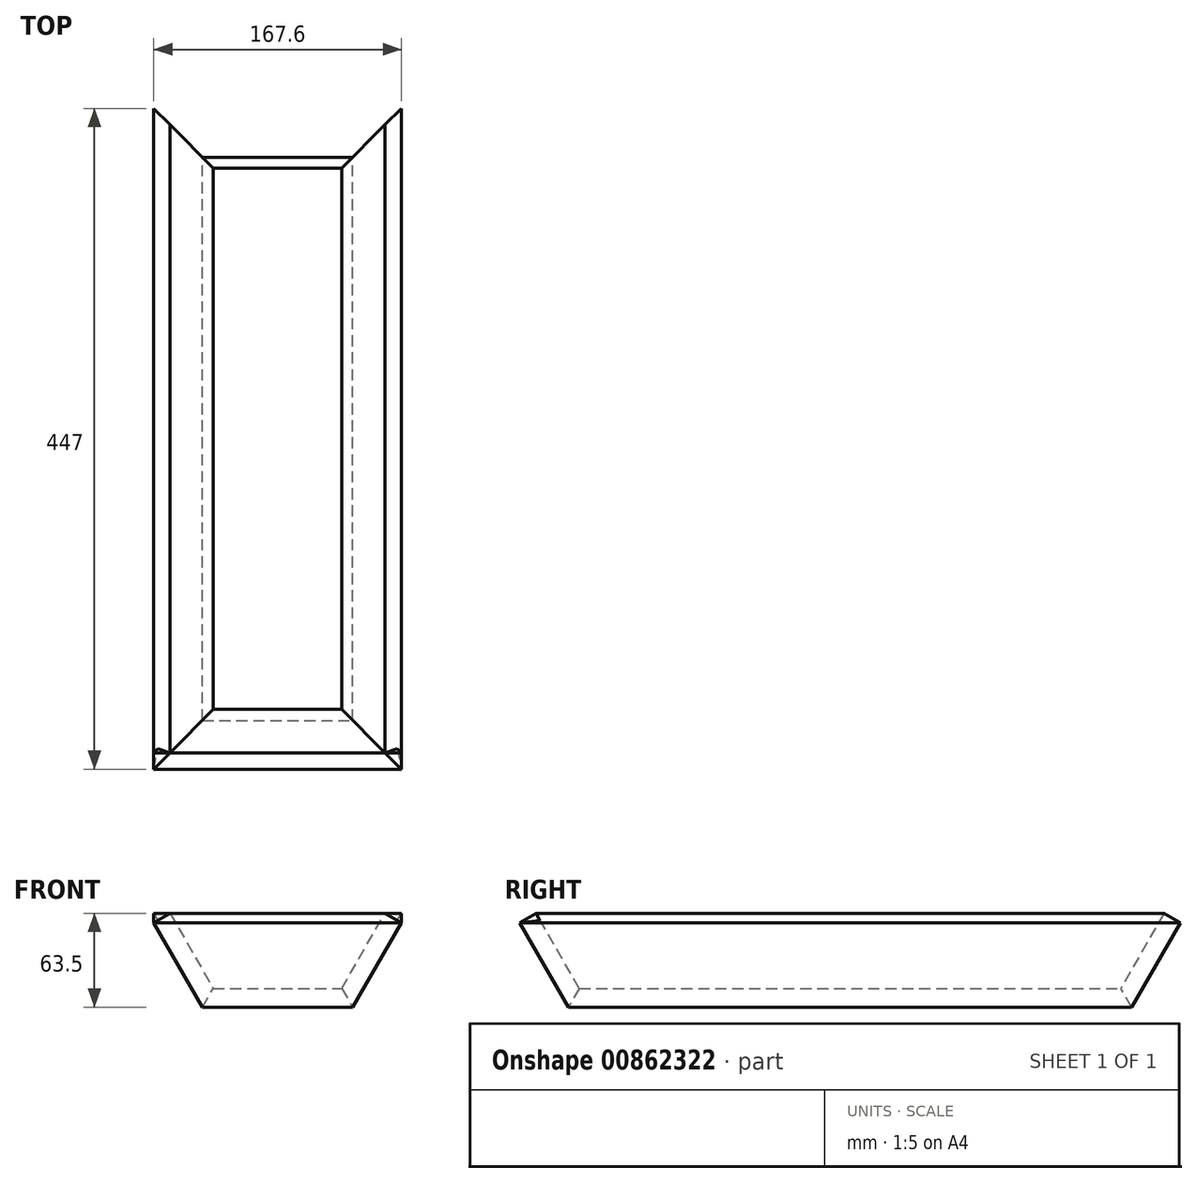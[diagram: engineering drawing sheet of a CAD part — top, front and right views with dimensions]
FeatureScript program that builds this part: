
annotation { "Feature Type Name" : "Feature", "Feature Type Description" : "" }
export const myFeature = defineFeature(function(context is Context, id is Id, definition is map)
    precondition{}
    {
        {
            var Q0;
            Q0=qCreatedBy(makeId("Top.planeOp"),FACE);
            var sketch = newSketch(context, id + "F0", { "sketchPlane" : qUnion([Q0])});
            skLineSegment(sketch, "E0.bottom", {"start": v(-50.8, 190.5) * mm, "end": v(50.8, 190.5) * mm});
            skLineSegment(sketch, "E0.top", {"start": v(-50.8, -190.5) * mm, "end": v(50.8, -190.5) * mm});
            skLineSegment(sketch, "E0.left", {"start": v(-50.8, 190.5) * mm, "end": v(-50.8, -190.5) * mm});
            skLineSegment(sketch, "E0.right", {"start": v(50.8, 190.5) * mm, "end": v(50.8, -190.5) * mm});
            skLineSegment(sketch, "E1", {"start": v(50.8, -190.5) * mm, "end": v(-50.8, 190.5) * mm, "construction": true});
            skSolve(sketch);
        }
        {
            var Q0;
            Q0 = qSketchRegion(id + "F0", true);
            extrude(context, id + "F1", {"entities" : qUnion([Q0]), "depth" : 12.7 * mm, "offsetDistance" : 25.4 * mm, "hasDraft" : true, "draftAngle" : 30 * degree, "draftPullDirection" : true});
        }
        {
            var Q0;
            Q0=qCreatedBy(makeId("Front.planeOp"),FACE);
            var sketch = newSketch(context, id + "F2", { "sketchPlane" : qUnion([Q0])});
            skLineSegment(sketch, "E2", {"start": v(-50.8, 0) * mm, "end": v(-83.8, 57.15) * mm});
            skLineSegment(sketch, "E3", {"start": v(-83.8, 57.15) * mm, "end": v(-72.8, 63.5) * mm});
            skLineSegment(sketch, "E4", {"start": v(-72.8, 63.5) * mm, "end": v(-43.47, 12.7) * mm});
            skLineSegment(sketch, "E5", {"start": v(-43.47, 12.7) * mm, "end": v(-50.8, 0) * mm});
            skSolve(sketch);
        }
        {
            var Q0;
            Q0 = qSketchRegion(id + "F2", true);
            extrude(context, id + "F3", {"entities" : qUnion([Q0]), "endBound" : BoundingType.SYMMETRIC, "depth" : 457.2 * mm, "offsetDistance" : 25.4 * mm, "hasSecondDirection" : true, "secondDirectionOppositeDirection" : true, "secondDirectionDepth" : 50.8 * mm});
        }
        {
            var Q0;
            Q0=makeQuery(id+"F1.opExtrude","CAP_FACE",FACE,{"disambiguationData":[OSD([sQuery(id+"F0.wireOp",EDGE,"E0.bottom"),sQuery(id+"F0.wireOp",EDGE,"E0.top"),sQuery(id+"F0.wireOp",EDGE,"E0.left"),sQuery(id+"F0.wireOp",EDGE,"E0.right")])],"isStart":true});
            var sketch = newSketch(context, id + "F4", { "sketchPlane" : qUnion([Q0])});
            skLineSegment(sketch, "E6", {"start": v(-43.47, -183.17) * mm, "end": v(-274.53, -414.23) * mm});
            skLineSegment(sketch, "E7", {"start": v(-274.53, -414.23) * mm, "end": v(-274.53, 414.23) * mm});
            skLineSegment(sketch, "E8", {"start": v(-274.53, 414.23) * mm, "end": v(-43.47, 183.17) * mm});
            skLineSegment(sketch, "E9", {"start": v(-43.47, 183.17) * mm, "end": v(-43.47, -183.17) * mm});
            skLineSegment(sketch, "E10", {"start": v(-274.53, -414.23) * mm, "end": v(274.53, -414.23) * mm});
            skLineSegment(sketch, "E11", {"start": v(274.53, -414.23) * mm, "end": v(43.47, -183.17) * mm});
            skLineSegment(sketch, "E12", {"start": v(43.47, -183.17) * mm, "end": v(43.47, 183.17) * mm});
            skLineSegment(sketch, "E13", {"start": v(43.47, 183.17) * mm, "end": v(-43.47, 183.17) * mm});
            skLineSegment(sketch, "E14", {"start": v(43.47, 183.17) * mm, "end": v(274.53, 414.23) * mm});
            skLineSegment(sketch, "E15", {"start": v(274.53, 414.23) * mm, "end": v(274.53, -414.23) * mm});
            skLineSegment(sketch, "E16", {"start": v(-274.53, 414.23) * mm, "end": v(274.53, 414.23) * mm});
            skLineSegment(sketch, "E17", {"start": v(-43.47, -183.17) * mm, "end": v(43.47, -183.17) * mm});
            skSolve(sketch);
        }
        {
            var Q0;
            {var subQ2=sQuery(id+"F4.wireOp",EDGE,"E10");Q0=makeQuery(id+"F4.imprint","IMPRINT",FACE,{"disambiguationData":[TD([[makeQuery(id+"F4.imprint","IMPRINT",EDGE,{"derivedFrom":subQ2}),1.0]])]});}
            var Q1;
            {var subQ2=sQuery(id+"F4.wireOp",EDGE,"E15");Q1=makeQuery(id+"F4.imprint","IMPRINT",FACE,{"disambiguationData":[TD([[makeQuery(id+"F4.imprint","IMPRINT",EDGE,{"derivedFrom":subQ2}),-1.0]])]});}
            var Q2;
            {var subQ2=sQuery(id+"F4.wireOp",EDGE,"E16");Q2=makeQuery(id+"F4.imprint","IMPRINT",FACE,{"disambiguationData":[TD([[makeQuery(id+"F4.imprint","IMPRINT",EDGE,{"derivedFrom":subQ2}),-1.0]])]});}
            extrude(context, id + "F5", {"entities" : qUnion([Q0, Q1, Q2]), "operationType" : NewBodyOperationType.REMOVE, "endBound" : BoundingType.THROUGH_ALL, "oppositeDirection" : true, "depth" : 25.4 * mm, "offsetDistance" : 25.4 * mm});
        }
        {
            var Q0;
            Q0=makeQuery(id+"F5.boolean.opBoolean","COPY",FACE,{"derivedFrom":makeQuery(id+"F5.opExtrude","SWEPT_FACE",FACE,{"disambiguationData":[OSD([sQuery(id+"F4.wireOp",EDGE,"E8")])]})});
            var sketch = newSketch(context, id + "F6", { "sketchPlane" : qUnion([Q0])});
            skLineSegment(sketch, "E18", {"start": v(-201.73, 63.5) * mm, "end": v(-160.26, 12.7) * mm});
            skLineSegment(sketch, "E19", {"start": v(-160.26, 12.7) * mm, "end": v(-170.62, 0) * mm});
            skLineSegment(sketch, "E20", {"start": v(-170.62, 0) * mm, "end": v(-217.29, 57.15) * mm});
            skLineSegment(sketch, "E21", {"start": v(-217.29, 57.15) * mm, "end": v(-201.73, 63.5) * mm});
            skSolve(sketch);
        }
        {
            var Q0;
            Q0 = qSketchRegion(id + "F6", true);
            extrude(context, id + "F7", {"entities" : qUnion([Q0]), "operationType" : NewBodyOperationType.REMOVE, "depth" : 25.4 * mm, "offsetDistance" : 25.4 * mm});
        }
        {
            var Q0;
            Q0=makeQuery(id+"F5.boolean.opBoolean","COPY",FACE,{"derivedFrom":makeQuery(id+"F5.opExtrude","SWEPT_FACE",FACE,{"disambiguationData":[OSD([sQuery(id+"F4.wireOp",EDGE,"E6")])]})});
            var sketch = newSketch(context, id + "F8", { "sketchPlane" : qUnion([Q0])});
            skLineSegment(sketch, "E22", {"start": v(201.73, 63.5) * mm, "end": v(217.29, 57.15) * mm});
            skLineSegment(sketch, "E23", {"start": v(217.29, 57.15) * mm, "end": v(170.62, 0) * mm});
            skLineSegment(sketch, "E24", {"start": v(170.62, 0) * mm, "end": v(160.26, 12.7) * mm});
            skLineSegment(sketch, "E25", {"start": v(160.26, 12.7) * mm, "end": v(201.73, 63.5) * mm});
            skSolve(sketch);
        }
        {
            var Q0;
            Q0 = qSketchRegion(id + "F8", true);
            extrude(context, id + "F9", {"entities" : qUnion([Q0]), "operationType" : NewBodyOperationType.REMOVE, "depth" : 25.4 * mm, "offsetDistance" : 25.4 * mm});
        }
        {
            var Q0;
            Q0=makeQuery(id+"F3.opExtrude","SWEPT_BODY",BODY,{"disambiguationData":[OSD([sQuery(id+"F2.wireOp",EDGE,"E2"),sQuery(id+"F2.wireOp",EDGE,"E3"),sQuery(id+"F2.wireOp",EDGE,"E4"),sQuery(id+"F2.wireOp",EDGE,"E5")])]});
            var Q1;
            Q1=qCreatedBy(makeId("Right.planeOp"),FACE);
            mirror(context, id + "F10", {"entities" : qUnion([Q0]), "mirrorPlane" : qUnion([Q1])});
        }
        {
            var Q0;
            Q0=makeQuery(id+"F1.opExtrude","CAP_VERTEX",VERTEX,{"disambiguationData":[OSD([sQuery(id+"F0.wireOp",EDGE,"E0.bottom"),sQuery(id+"F0.wireOp",EDGE,"E0.right")])],"isStart":true});
            var Q1;
            Q1=makeQuery(id+"F1.opExtrude","CAP_VERTEX",VERTEX,{"disambiguationData":[OSD([sQuery(id+"F0.wireOp",EDGE,"E0.bottom"),sQuery(id+"F0.wireOp",EDGE,"E0.left")])],"isStart":true});
            var Q2;
            Q2=makeQuery(id+"F5.boolean.opBoolean","INTERSECT",VERTEX,{"derivedFrom":[makeQuery(id+"F3.opExtrude","SWEPT_FACE",FACE,{"disambiguationData":[OSD([sQuery(id+"F2.wireOp",EDGE,"E2")])]}),makeQuery(id+"F3.opExtrude","SWEPT_FACE",FACE,{"disambiguationData":[OSD([sQuery(id+"F2.wireOp",EDGE,"E3")])]}),makeQuery(id+"F5.opExtrude","SWEPT_FACE",FACE,{"disambiguationData":[OSD([sQuery(id+"F4.wireOp",EDGE,"E6")])]})]});
            cPlane(context, id + "F11", {"entities" : qUnion([Q0, Q1, Q2]), "cplaneType" : CPlaneType.THREE_POINT, "offset" : 25.4 * mm, "width" : 152.4 * mm, "height" : 152.4 * mm});
        }
        {
            var Q0;
            Q0=qCreatedBy(id+"F11.planeOp",FACE);
            var sketch = newSketch(context, id + "F12", { "sketchPlane" : qUnion([Q0])});
            skLineSegment(sketch, "E26", {"start": v(-83.8, 161.24) * mm, "end": v(-50.8, 95.25) * mm});
            skLineSegment(sketch, "E27", {"start": v(-50.8, 95.25) * mm, "end": v(50.8, 95.25) * mm});
            skLineSegment(sketch, "E28", {"start": v(50.8, 95.25) * mm, "end": v(83.8, 161.24) * mm});
            skLineSegment(sketch, "E29", {"start": v(83.8, 161.24) * mm, "end": v(-83.8, 161.24) * mm});
            skSolve(sketch);
        }
        {
            var Q0;
            Q0 = qSketchRegion(id + "F12", true);
            extrude(context, id + "F13", {"entities" : qUnion([Q0]), "depth" : 12.7 * mm, "offsetDistance" : 25.4 * mm});
        }
        {
            var Q0;
            Q0=makeQuery(id+"F1.opExtrude","SWEPT_BODY",BODY,{"disambiguationData":[OSD([sQuery(id+"F0.wireOp",EDGE,"E0.bottom"),sQuery(id+"F0.wireOp",EDGE,"E0.top"),sQuery(id+"F0.wireOp",EDGE,"E0.left"),sQuery(id+"F0.wireOp",EDGE,"E0.right")])]});
            var Q1;
            Q1=makeQuery(id+"F10.opPattern","COPY",BODY,{"derivedFrom":makeQuery(id+"F3.opExtrude","SWEPT_BODY",BODY,{"disambiguationData":[OSD([sQuery(id+"F2.wireOp",EDGE,"E2"),sQuery(id+"F2.wireOp",EDGE,"E3"),sQuery(id+"F2.wireOp",EDGE,"E4"),sQuery(id+"F2.wireOp",EDGE,"E5")])]}),"instanceName":"1"});
            var Q2;
            Q2=makeQuery(id+"F3.opExtrude","SWEPT_BODY",BODY,{"disambiguationData":[OSD([sQuery(id+"F2.wireOp",EDGE,"E2"),sQuery(id+"F2.wireOp",EDGE,"E3"),sQuery(id+"F2.wireOp",EDGE,"E4"),sQuery(id+"F2.wireOp",EDGE,"E5")])]});
            var Q3;
            Q3=makeQuery(id+"F13.opExtrude","SWEPT_BODY",BODY,{"disambiguationData":[OSD([sQuery(id+"F12.wireOp",EDGE,"E26"),sQuery(id+"F12.wireOp",EDGE,"E27"),sQuery(id+"F12.wireOp",EDGE,"E28"),sQuery(id+"F12.wireOp",EDGE,"E29")])]});
            booleanBodies(context, id + "F14", {"operationType" : BooleanOperationType.SUBTRACTION, "tools" : qUnion([Q0, Q1, Q2]), "targets" : qUnion([Q3]), "keepTools" : true});
        }
        {
            var Q0;
            Q0=makeQuery(id+"F14.opBoolean","SPLIT",BODY,{"disambiguationData":[OD(0.0)],"derivedFrom":makeQuery(id+"F13.opExtrude","SWEPT_BODY",BODY,{"disambiguationData":[OSD([sQuery(id+"F12.wireOp",EDGE,"E26"),sQuery(id+"F12.wireOp",EDGE,"E27"),sQuery(id+"F12.wireOp",EDGE,"E28"),sQuery(id+"F12.wireOp",EDGE,"E29")])]})});
            var Q1;
            Q1=qCreatedBy(makeId("Front.planeOp"),FACE);
            mirror(context, id + "F15", {"entities" : qUnion([Q0]), "mirrorPlane" : qUnion([Q1])});
        }
        {
            var Q0;
            Q0=makeQuery(id+"F14.opBoolean","SPLIT",BODY,{"disambiguationData":[OD(2.0)],"derivedFrom":makeQuery(id+"F13.opExtrude","SWEPT_BODY",BODY,{"disambiguationData":[OSD([sQuery(id+"F12.wireOp",EDGE,"E26"),sQuery(id+"F12.wireOp",EDGE,"E27"),sQuery(id+"F12.wireOp",EDGE,"E28"),sQuery(id+"F12.wireOp",EDGE,"E29")])]})});
            var Q1;
            Q1=makeQuery(id+"F14.opBoolean","SPLIT",BODY,{"disambiguationData":[OD(1.0)],"derivedFrom":makeQuery(id+"F13.opExtrude","SWEPT_BODY",BODY,{"disambiguationData":[OSD([sQuery(id+"F12.wireOp",EDGE,"E26"),sQuery(id+"F12.wireOp",EDGE,"E27"),sQuery(id+"F12.wireOp",EDGE,"E28"),sQuery(id+"F12.wireOp",EDGE,"E29")])]})});
            deleteBodies(context, id + "F16", {"entities" : qUnion([Q0, Q1])});
        }
    });
